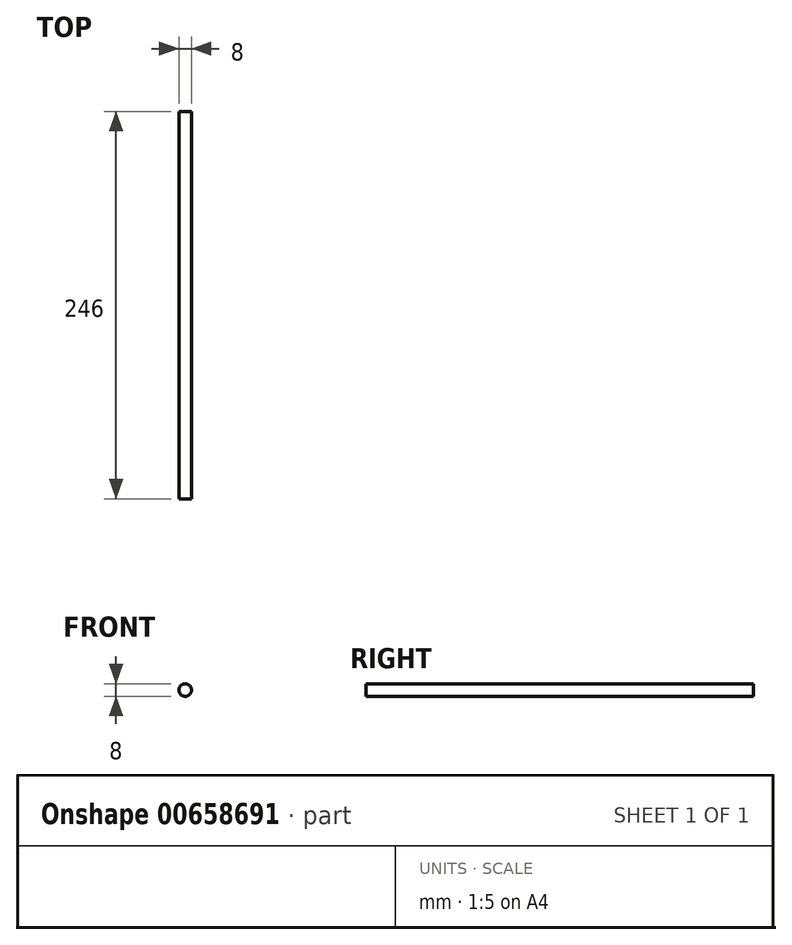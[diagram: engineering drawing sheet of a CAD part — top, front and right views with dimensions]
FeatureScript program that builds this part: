
annotation { "Feature Type Name" : "Feature", "Feature Type Description" : "" }
export const myFeature = defineFeature(function(context is Context, id is Id, definition is map)
    precondition{}
    {
        {
            var Q0;
            Q0=qCreatedBy(makeId("Front.planeOp"),FACE);
            var sketch = newSketch(context, id + "F0", { "sketchPlane" : qUnion([Q0])});
            skCircle(sketch, "E0", {"center": v(0, 0) * mm, "radius": 4 * mm});
            skSolve(sketch);
        }
        {
            var Q0;
            Q0=makeQuery(id+"F0.imprint","IMPRINT",FACE,{"disambiguationData":[TD([[makeQuery(id+"F0.imprint","IMPRINT",EDGE,{"derivedFrom":sQuery(id+"F0.wireOp",EDGE,"E0")}),1.0]])]});
            extrude(context, id + "F1", {"entities" : qUnion([Q0]), "depth" : 246 * mm, "symmetric" : true});
        }
    });
